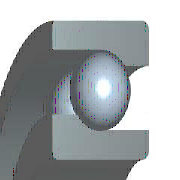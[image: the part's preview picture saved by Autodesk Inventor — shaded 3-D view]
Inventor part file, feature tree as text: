
AUTODESK INVENTOR PART (.ipt)
format: ipt  version: 2023.2 (Build 272271030, 271C)  size: 292,352 bytes
history: native  units: mm (DEFAULTED — no unit token found)
features: sketch x7, other x5, plane x3, fillet x2, pattern_circular x1
ambient origin geometry x8: Origin, YZ Plane, XZ Plane, XY Plane, X Axis, Y Axis, Z Axis, Center Point
bodies: Solid1 (feature_tree)
feature tree (18):
  plane  "WorkPlane1"
  plane  "Work Plane2"
  plane  "WorkPlane2"
  sketch  "Sketch1"  dims[d0=-15.0mm]
  other  "WorkPoint1"
  sketch  "Sketch2"  dims[d1=10.0mm]
  other  "WorkPoint3"
  sketch  "Sketch3"  dims[d2=12.5mm]
  other  "WorkPoint2"
  other  "WorkAxis1"
  sketch  "Sketch7"  dims[d6=15.0mm d7=360.0deg d8=7.0mm d9=7.5mm d10=8.1mm d11=8.1mm d12=360.0deg d13=4.05mm d14=4.05mm d15=360.0deg d16=70.0mm d18=360.0deg d19=0.6mm d20=1.0mm d21=38.5mm d22=33.64mm d23=43.36mm d26=0.0mm d27=0.0mm d28=0.0mm d29=0.0mm d30=0.0mm]
  other  "Work Axis2"
  pattern_circular  "PolarArray1"  Angle=360.0deg  [1 undecoded]
  fillet  "Fillet1"  Radius=7.0mm
  fillet  "Fillet2"  Radius=7.5mm
  sketch  "Sketch4"  dims[d3=23.5mm]
  sketch  "Sketch5"  dims[d4=26.0mm]
  sketch  "Sketch6"  dims[d5=14.0mm]
note: 1 required parameter value undecoded (feature->parameter linkage not recoverable at this tier; creation-order binding heuristic only, values carry confidence <= 0.55)
